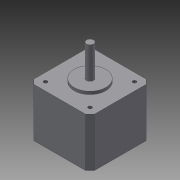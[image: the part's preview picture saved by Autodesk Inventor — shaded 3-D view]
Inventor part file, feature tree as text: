
AUTODESK INVENTOR PART (.ipt)
format: ipt  version: 2015 (Build 190159000, 159)  size: 112,640 bytes
history: native  units: in
note: dims shown in document units (in); Inventor stores cm internally (conversion verified against a paired STEP export)
features: sketch x4, extrude x3, hole x1
ambient origin geometry x8: Origin, YZ Plane, XZ Plane, XY Plane, X Axis, Y Axis, Z Axis, Center Point
bodies: Solid1 (feature_tree)
feature tree (8):
  extrude  "Extrusion1"  Depth=1.6654in
  extrude  "Extrusion2"  Depth=0.125in
  extrude  "Extrusion3"  Depth=0.125in
  hole  "Hole1"  [1 undecoded]
  sketch  "Sketch1"  dims[d0=1.6654in d1=1.6654in]
  sketch  "Sketch2"  dims[d2=0.125in d3=0.125in]
  sketch  "Sketch3"  dims[d4=0.125in d5=0.125in]
  sketch  "Sketch4"  dims[d6=0.125in d7=0.125in d8=0.125in d9=0.125in d10=1.3386in d11=0.0in d12=0.8661in d13=0.0787in d14=0.0in d15=0.1969in d16=0.8661in d17=0.0in d18=1.2205in d19=1.2205in d20=0.097in d21=0.1575in d22=0.375in d23=0.25in d24=0.5635in d25=0.1969in d26=0.8108in]
note: 1 required parameter value undecoded (feature->parameter linkage not recoverable at this tier; creation-order binding heuristic only, values carry confidence <= 0.55)
